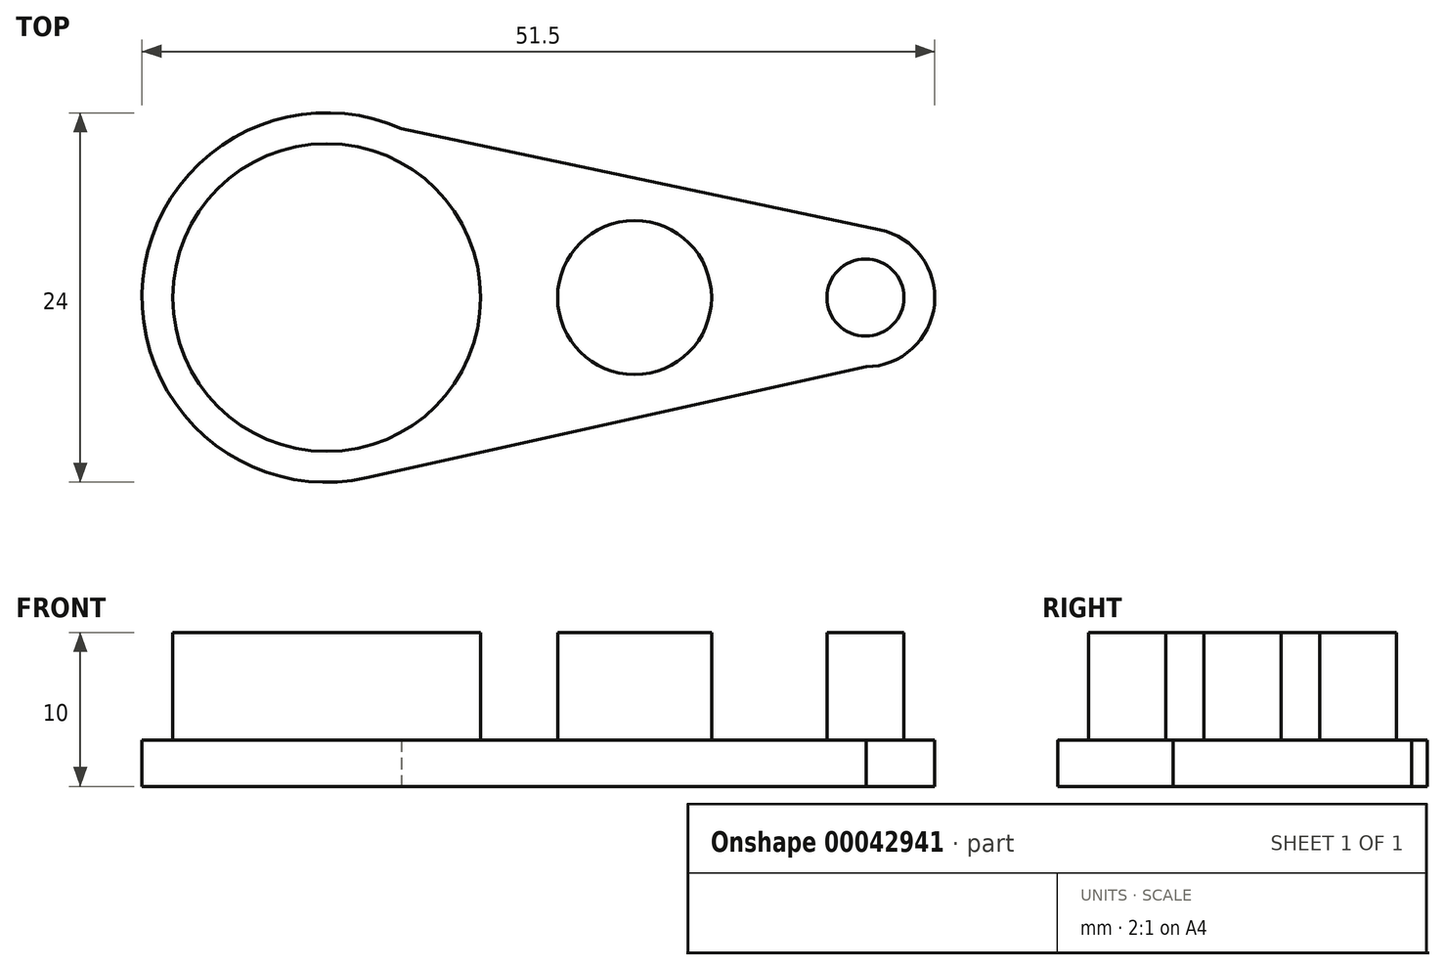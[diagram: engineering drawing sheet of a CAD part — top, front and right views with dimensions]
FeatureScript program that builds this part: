
annotation { "Feature Type Name" : "Feature", "Feature Type Description" : "" }
export const myFeature = defineFeature(function(context is Context, id is Id, definition is map)
    precondition{}
    {
        {
            var Q0;
            Q0=qCreatedBy(makeId("Top.planeOp"),FACE);
            var sketch = newSketch(context, id + "F0", { "sketchPlane" : qUnion([Q0])});
            skCircle(sketch, "E0", {"center": v(0, 0) * mm, "radius": 10 * mm});
            skCircle(sketch, "E1", {"center": v(20, 0) * mm, "radius": 5 * mm});
            skCircle(sketch, "E2", {"center": v(35, 0) * mm, "radius": 2.5 * mm});
            skArc(sketch, "E3.0", {"start": v(35.04, -4.5) * mm, "mid": v(39.48, -0.45) * mm, "end": v(35.93, 4.4) * mm});
            skArc(sketch, "E4.0", {"start": v(4.86, 10.97) * mm, "mid": v(-11.94, 1.19) * mm, "end": v(2.6, -11.71) * mm});
            skLineSegment(sketch, "E5", {"start": v(4.86, 10.97) * mm, "end": v(35.93, 4.4) * mm});
            skLineSegment(sketch, "E6", {"start": v(35.04, -4.5) * mm, "end": v(2.6, -11.71) * mm});
            skPoint(sketch, "E7.orphan", {"position": v(0, -12.3) * mm});
            skPoint(sketch, "E8.orphan", {"position": v(0, 12) * mm});
            skSolve(sketch);
        }
        {
            var Q0;
            Q0 = qSketchRegion(id + "F0", true);
            var Q1;
            Q1=makeQuery(id+"F0.imprint","IMPRINT",FACE,{"disambiguationData":[TD([[makeQuery(id+"F0.imprint","IMPRINT",EDGE,{"derivedFrom":sQuery(id+"F0.wireOp",EDGE,"E0")}),1.0]])]});
            var Q2;
            Q2=makeQuery(id+"F0.imprint","IMPRINT",FACE,{"disambiguationData":[TD([[makeQuery(id+"F0.imprint","IMPRINT",EDGE,{"derivedFrom":sQuery(id+"F0.wireOp",EDGE,"E1")}),1.0]])]});
            var Q3;
            Q3=makeQuery(id+"F0.imprint","IMPRINT",FACE,{"disambiguationData":[TD([[makeQuery(id+"F0.imprint","IMPRINT",EDGE,{"derivedFrom":sQuery(id+"F0.wireOp",EDGE,"E2")}),1.0]])]});
            extrude(context, id + "F1", {"entities" : qUnion([Q0, Q1, Q2, Q3]), "depth" : 3 * mm});
        }
        {
            var Q0;
            Q0=makeQuery(id+"F0.imprint","IMPRINT",FACE,{"disambiguationData":[TD([[makeQuery(id+"F0.imprint","IMPRINT",EDGE,{"derivedFrom":sQuery(id+"F0.wireOp",EDGE,"E0")}),1.0]])]});
            var Q1;
            Q1=makeQuery(id+"F0.imprint","IMPRINT",FACE,{"disambiguationData":[TD([[makeQuery(id+"F0.imprint","IMPRINT",EDGE,{"derivedFrom":sQuery(id+"F0.wireOp",EDGE,"E1")}),1.0]])]});
            var Q2;
            Q2=makeQuery(id+"F0.imprint","IMPRINT",FACE,{"disambiguationData":[TD([[makeQuery(id+"F0.imprint","IMPRINT",EDGE,{"derivedFrom":sQuery(id+"F0.wireOp",EDGE,"E2")}),1.0]])]});
            extrude(context, id + "F2", {"entities" : qUnion([Q0, Q1, Q2]), "operationType" : NewBodyOperationType.ADD, "depth" : 10 * mm});
        }
    });
